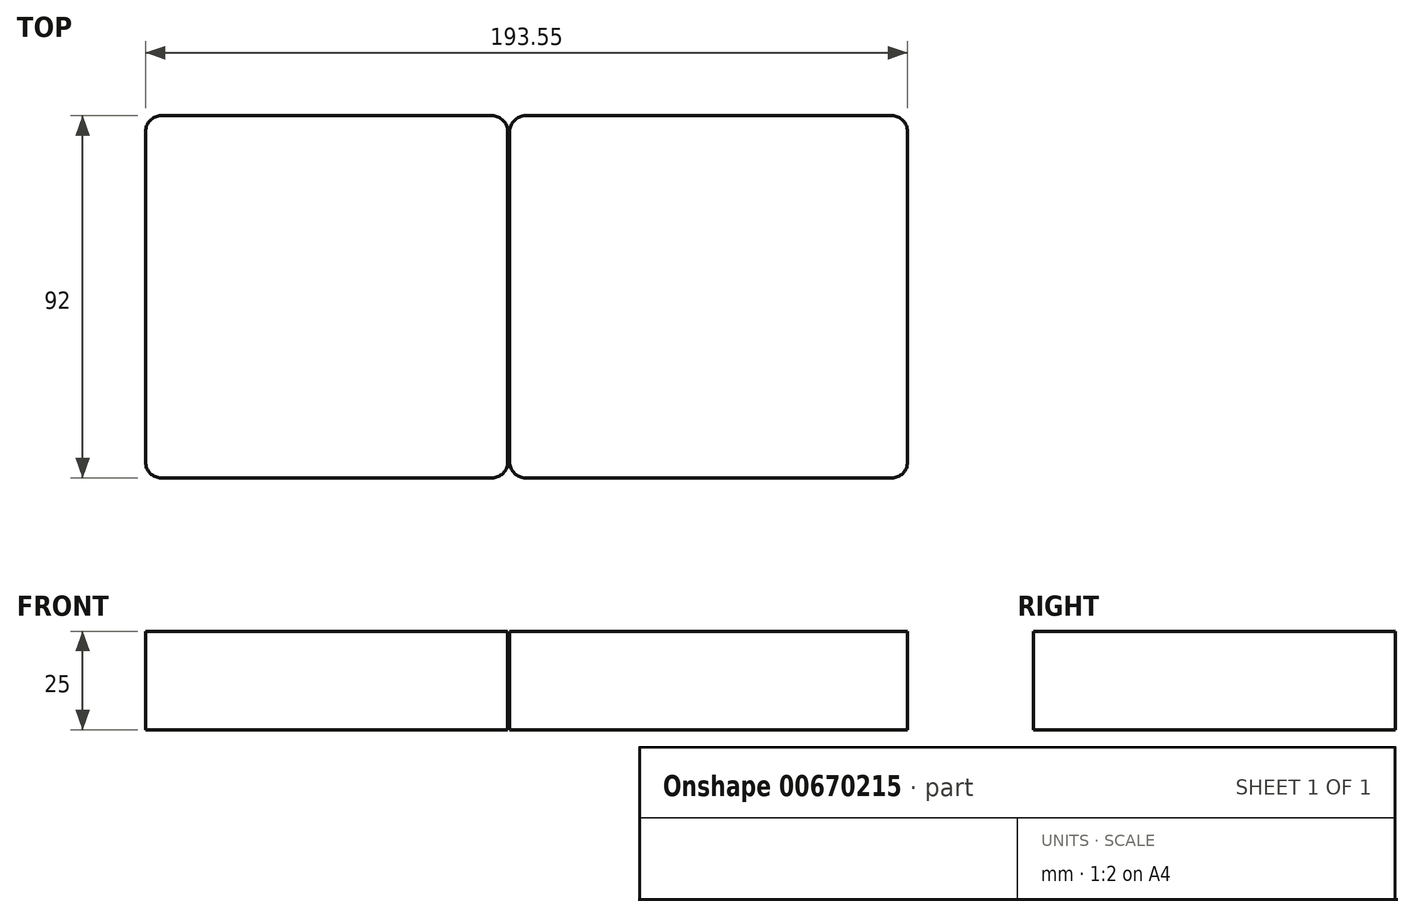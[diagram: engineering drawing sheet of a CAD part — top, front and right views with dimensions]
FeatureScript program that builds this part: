
annotation { "Feature Type Name" : "Feature", "Feature Type Description" : "" }
export const myFeature = defineFeature(function(context is Context, id is Id, definition is map)
    precondition{}
    {
        {
            var Q0;
            Q0=qCreatedBy(makeId("Top.planeOp"),FACE);
            var sketch = newSketch(context, id + "F0", { "sketchPlane" : qUnion([Q0])});
            skLineSegment(sketch, "E0.bottom", {"start": v(4, 0) * mm, "end": v(88, 0) * mm});
            skLineSegment(sketch, "E0.top", {"start": v(4, 92) * mm, "end": v(88, 92) * mm});
            skLineSegment(sketch, "E0.left", {"start": v(0, 4) * mm, "end": v(0, 88) * mm});
            skLineSegment(sketch, "E0.right", {"start": v(92, 4) * mm, "end": v(92, 88) * mm});
            skLineSegment(sketch, "E1.bottom", {"start": v(96.5, 92) * mm, "end": v(189.55, 92) * mm});
            skLineSegment(sketch, "E1.top", {"start": v(96.5, 0) * mm, "end": v(189.55, 0) * mm});
            skLineSegment(sketch, "E1.left", {"start": v(92.5, 88) * mm, "end": v(92.5, 4) * mm});
            skLineSegment(sketch, "E1.right", {"start": v(193.55, 88) * mm, "end": v(193.55, 4) * mm});
            skPoint(sketch, "E2.visualSharp", {"position": v(0, 92) * mm});
            skArc(sketch, "E2.filletArc", {"start": v(4, 92) * mm, "mid": v(1.17, 90.83) * mm, "end": v(0, 88) * mm});
            skPoint(sketch, "E3.visualSharp", {"position": v(92, 92) * mm});
            skArc(sketch, "E3.filletArc", {"start": v(92, 88) * mm, "mid": v(90.83, 90.83) * mm, "end": v(88, 92) * mm});
            skPoint(sketch, "E4.visualSharp", {"position": v(92, 0) * mm});
            skArc(sketch, "E4.filletArc", {"start": v(88, 0) * mm, "mid": v(90.83, 1.17) * mm, "end": v(92, 4) * mm});
            skPoint(sketch, "E5.visualSharp", {"position": v(92.5, 0) * mm});
            skArc(sketch, "E5.filletArc", {"start": v(92.5, 4) * mm, "mid": v(93.67, 1.17) * mm, "end": v(96.5, 0) * mm});
            skPoint(sketch, "E6.visualSharp", {"position": v(92.5, 92) * mm});
            skArc(sketch, "E6.filletArc", {"start": v(96.5, 92) * mm, "mid": v(93.67, 90.83) * mm, "end": v(92.5, 88) * mm});
            skPoint(sketch, "E7.visualSharp", {"position": v(0, 0) * mm});
            skArc(sketch, "E7.filletArc", {"start": v(0, 4) * mm, "mid": v(1.17, 1.17) * mm, "end": v(4, 0) * mm});
            skPoint(sketch, "E8.visualSharp", {"position": v(193.55, 92) * mm});
            skArc(sketch, "E8.filletArc", {"start": v(193.55, 88) * mm, "mid": v(192.38, 90.83) * mm, "end": v(189.55, 92) * mm});
            skPoint(sketch, "E9.visualSharp", {"position": v(193.55, 0) * mm});
            skArc(sketch, "E9.filletArc", {"start": v(189.55, 0) * mm, "mid": v(192.38, 1.17) * mm, "end": v(193.55, 4) * mm});
            skSolve(sketch);
        }
        {
            var Q0;
            Q0 = qSketchRegion(id + "F0", true);
            extrude(context, id + "F1", {"entities" : qUnion([Q0]), "depth" : 25 * mm, "offsetDistance" : 25 * mm});
        }
    });
